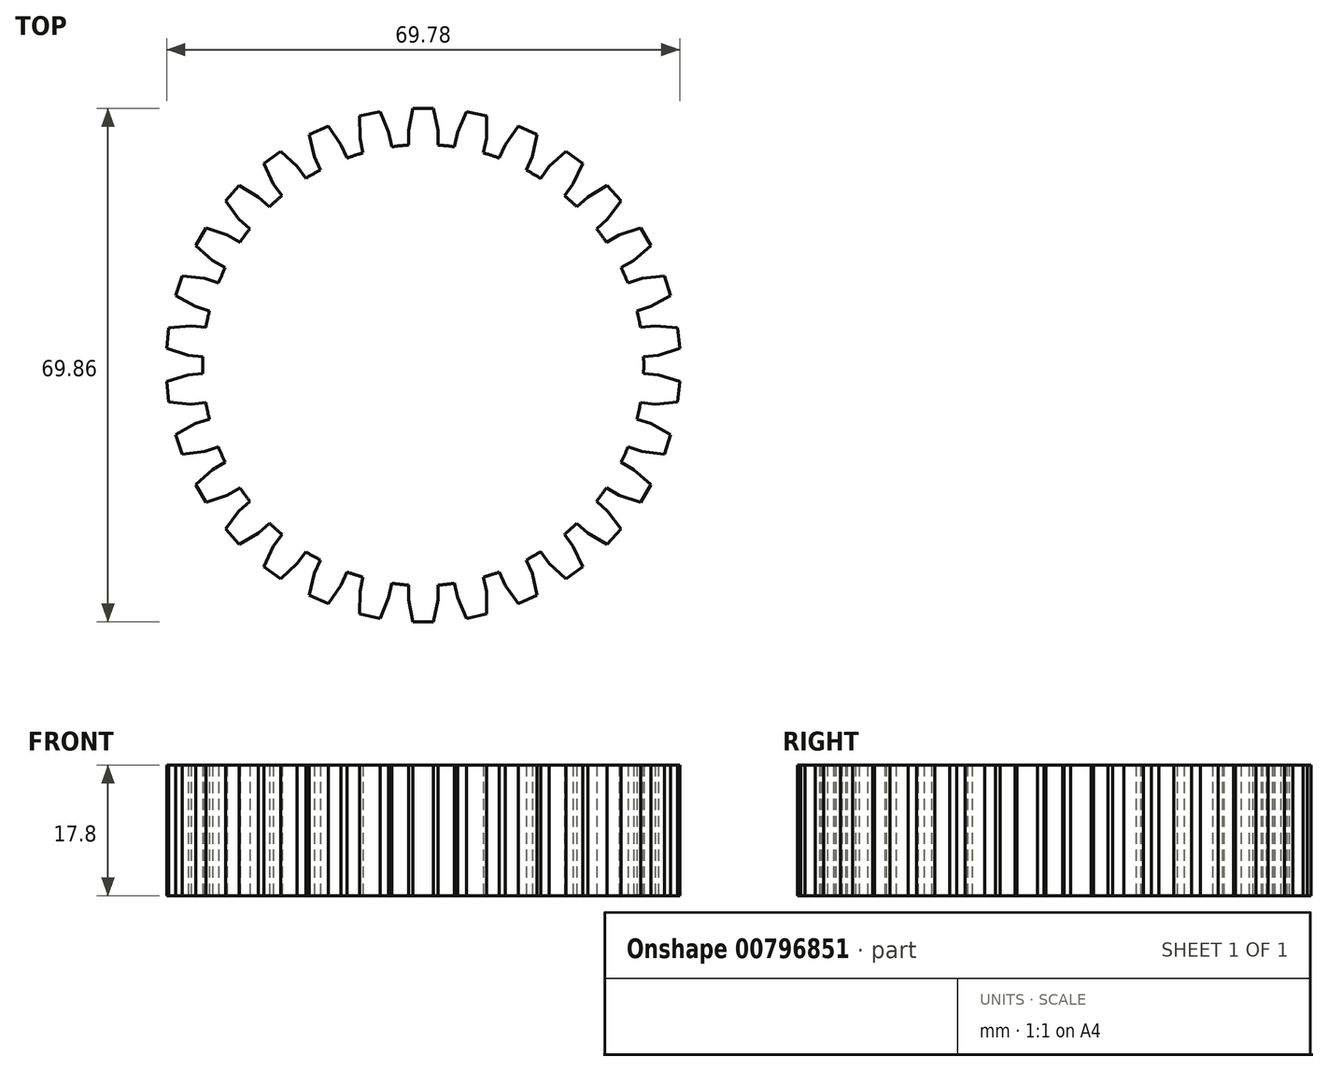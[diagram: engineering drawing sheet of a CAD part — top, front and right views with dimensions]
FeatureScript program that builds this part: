
annotation { "Feature Type Name" : "Feature", "Feature Type Description" : "" }
export const myFeature = defineFeature(function(context is Context, id is Id, definition is map)
    precondition{}
    {
        {
            var Q0;
            Q0=qCreatedBy(makeId("Top.planeOp"),FACE);
            var sketch = newSketch(context, id + "F0", { "sketchPlane" : qUnion([Q0])});
            skArc(sketch, "E0", {"start": v(-23.58, 18.54) * mm, "mid": v(-24.27, 17.63) * mm, "end": v(-24.92, 16.7) * mm});
            skLineSegment(sketch, "E1", {"start": v(1.41, 34.93) * mm, "end": v(-1.41, 34.93) * mm});
            skLineSegment(sketch, "E2", {"start": v(-2, 31.93) * mm, "end": v(-2, 29.93) * mm});
            skLineSegment(sketch, "E3", {"start": v(2, 31.93) * mm, "end": v(2, 29.93) * mm});
            skLineSegment(sketch, "E4", {"start": v(-2, 31.93) * mm, "end": v(-1.41, 34.93) * mm});
            skLineSegment(sketch, "E5.MirrorCS", {"start": v(2, 31.93) * mm, "end": v(1.41, 34.93) * mm});
            skPoint(sketch, "E6.orphan", {"position": v(-1.36, 35.2) * mm});
            skPoint(sketch, "E7.orphan", {"position": v(1.36, 35.2) * mm});
            skPoint(sketch, "E8.1.0", {"position": v(-8.65, 34.15) * mm});
            skLineSegment(sketch, "E8.1.1", {"start": v(-4.68, 31.65) * mm, "end": v(-5.88, 34.46) * mm});
            skLineSegment(sketch, "E8.1.2", {"start": v(-8.6, 30.82) * mm, "end": v(-8.64, 33.88) * mm});
            skLineSegment(sketch, "E8.1.3", {"start": v(-4.68, 31.65) * mm, "end": v(-4.27, 29.7) * mm});
            skLineSegment(sketch, "E8.1.4", {"start": v(-8.6, 30.82) * mm, "end": v(-8.18, 28.86) * mm});
            skLineSegment(sketch, "E8.1.5", {"start": v(-5.88, 34.46) * mm, "end": v(-8.64, 33.88) * mm});
            skPoint(sketch, "E8.1.6", {"position": v(-5.99, 34.71) * mm});
            skPoint(sketch, "E8.2.0", {"position": v(-15.56, 31.6) * mm});
            skLineSegment(sketch, "E8.2.1", {"start": v(-11.16, 29.99) * mm, "end": v(-12.92, 32.49) * mm});
            skLineSegment(sketch, "E8.2.2", {"start": v(-14.82, 28.36) * mm, "end": v(-15.5, 31.34) * mm});
            skLineSegment(sketch, "E8.2.3", {"start": v(-11.16, 29.99) * mm, "end": v(-10.35, 28.16) * mm});
            skLineSegment(sketch, "E8.2.4", {"start": v(-14.82, 28.36) * mm, "end": v(-14, 26.53) * mm});
            skLineSegment(sketch, "E8.2.5", {"start": v(-12.92, 32.49) * mm, "end": v(-15.5, 31.34) * mm});
            skPoint(sketch, "E8.2.6", {"position": v(-13.08, 32.7) * mm});
            skPoint(sketch, "E8.3.0", {"position": v(-21.79, 27.68) * mm});
            skLineSegment(sketch, "E8.3.1", {"start": v(-17.15, 27.01) * mm, "end": v(-19.4, 29.1) * mm});
            skLineSegment(sketch, "E8.3.2", {"start": v(-20.39, 24.66) * mm, "end": v(-21.67, 27.43) * mm});
            skLineSegment(sketch, "E8.3.3", {"start": v(-17.15, 27.01) * mm, "end": v(-15.98, 25.4) * mm});
            skLineSegment(sketch, "E8.3.4", {"start": v(-20.39, 24.66) * mm, "end": v(-19.21, 23.04) * mm});
            skLineSegment(sketch, "E8.3.5", {"start": v(-19.4, 29.1) * mm, "end": v(-21.67, 27.43) * mm});
            skPoint(sketch, "E8.3.6", {"position": v(-19.6, 29.27) * mm});
            skPoint(sketch, "E8.4.0", {"position": v(-27.07, 22.54) * mm});
            skLineSegment(sketch, "E8.4.1", {"start": v(-22.4, 22.85) * mm, "end": v(-25.02, 24.42) * mm});
            skLineSegment(sketch, "E8.4.2", {"start": v(-25.07, 19.88) * mm, "end": v(-26.9, 22.33) * mm});
            skLineSegment(sketch, "E8.4.3", {"start": v(-22.4, 22.85) * mm, "end": v(-20.9, 21.52) * mm});
            skLineSegment(sketch, "E8.4.4", {"start": v(-25.07, 19.88) * mm, "end": v(-23.58, 18.54) * mm});
            skLineSegment(sketch, "E8.4.5", {"start": v(-25.02, 24.42) * mm, "end": v(-26.9, 22.33) * mm});
            skPoint(sketch, "E8.4.6", {"position": v(-25.25, 24.56) * mm});
            skPoint(sketch, "E8.5.0", {"position": v(-31.16, 16.42) * mm});
            skLineSegment(sketch, "E8.5.1", {"start": v(-26.66, 17.7) * mm, "end": v(-29.55, 18.69) * mm});
            skLineSegment(sketch, "E8.5.2", {"start": v(-28.66, 14.23) * mm, "end": v(-30.96, 16.25) * mm});
            skLineSegment(sketch, "E8.5.3", {"start": v(-26.66, 17.7) * mm, "end": v(-24.92, 16.7) * mm});
            skLineSegment(sketch, "E8.5.4", {"start": v(-28.66, 14.23) * mm, "end": v(-26.92, 13.23) * mm});
            skLineSegment(sketch, "E8.5.5", {"start": v(-29.55, 18.69) * mm, "end": v(-30.96, 16.25) * mm});
            skPoint(sketch, "E8.5.6", {"position": v(-29.8, 18.78) * mm});
            skPoint(sketch, "E8.6.0", {"position": v(-33.9, 9.59) * mm});
            skLineSegment(sketch, "E8.6.1", {"start": v(-29.75, 11.77) * mm, "end": v(-32.79, 12.14) * mm});
            skLineSegment(sketch, "E8.6.2", {"start": v(-30.99, 7.97) * mm, "end": v(-33.66, 9.45) * mm});
            skLineSegment(sketch, "E8.6.3", {"start": v(-29.75, 11.77) * mm, "end": v(-27.85, 11.15) * mm});
            skLineSegment(sketch, "E8.6.4", {"start": v(-30.99, 7.97) * mm, "end": v(-29.09, 7.35) * mm});
            skLineSegment(sketch, "E8.6.5", {"start": v(-32.79, 12.14) * mm, "end": v(-33.66, 9.45) * mm});
            skPoint(sketch, "E8.6.6", {"position": v(-33.06, 12.17) * mm});
            skPoint(sketch, "E8.7.0", {"position": v(-35.15, 2.33) * mm});
            skLineSegment(sketch, "E8.7.1", {"start": v(-31.55, 5.33) * mm, "end": v(-34.6, 5.05) * mm});
            skLineSegment(sketch, "E8.7.2", {"start": v(-31.97, 1.35) * mm, "end": v(-34.89, 2.25) * mm});
            skLineSegment(sketch, "E8.7.3", {"start": v(-31.55, 5.33) * mm, "end": v(-29.56, 5.12) * mm});
            skLineSegment(sketch, "E8.7.4", {"start": v(-31.97, 1.35) * mm, "end": v(-29.98, 1.14) * mm});
            skLineSegment(sketch, "E8.7.5", {"start": v(-34.6, 5.05) * mm, "end": v(-34.89, 2.25) * mm});
            skPoint(sketch, "E8.7.6", {"position": v(-34.86, 5.03) * mm});
            skPoint(sketch, "E8.8.0", {"position": v(-34.86, -5.03) * mm});
            skLineSegment(sketch, "E8.8.1", {"start": v(-31.97, -1.35) * mm, "end": v(-34.89, -2.25) * mm});
            skLineSegment(sketch, "E8.8.2", {"start": v(-31.55, -5.33) * mm, "end": v(-34.6, -5.05) * mm});
            skLineSegment(sketch, "E8.8.3", {"start": v(-31.97, -1.35) * mm, "end": v(-29.98, -1.14) * mm});
            skLineSegment(sketch, "E8.8.4", {"start": v(-31.55, -5.33) * mm, "end": v(-29.56, -5.12) * mm});
            skLineSegment(sketch, "E8.8.5", {"start": v(-34.89, -2.25) * mm, "end": v(-34.6, -5.05) * mm});
            skPoint(sketch, "E8.8.6", {"position": v(-35.15, -2.33) * mm});
            skPoint(sketch, "E8.9.0", {"position": v(-33.06, -12.17) * mm});
            skLineSegment(sketch, "E8.9.1", {"start": v(-30.99, -7.97) * mm, "end": v(-33.66, -9.45) * mm});
            skLineSegment(sketch, "E8.9.2", {"start": v(-29.75, -11.77) * mm, "end": v(-32.79, -12.14) * mm});
            skLineSegment(sketch, "E8.9.3", {"start": v(-30.99, -7.97) * mm, "end": v(-29.09, -7.35) * mm});
            skLineSegment(sketch, "E8.9.4", {"start": v(-29.75, -11.77) * mm, "end": v(-27.85, -11.15) * mm});
            skLineSegment(sketch, "E8.9.5", {"start": v(-33.66, -9.45) * mm, "end": v(-32.79, -12.14) * mm});
            skPoint(sketch, "E8.9.6", {"position": v(-33.9, -9.59) * mm});
            skPoint(sketch, "E8.10.0", {"position": v(-29.8, -18.78) * mm});
            skLineSegment(sketch, "E8.10.1", {"start": v(-28.66, -14.23) * mm, "end": v(-30.96, -16.25) * mm});
            skLineSegment(sketch, "E8.10.2", {"start": v(-26.66, -17.7) * mm, "end": v(-29.55, -18.69) * mm});
            skLineSegment(sketch, "E8.10.3", {"start": v(-28.66, -14.23) * mm, "end": v(-26.92, -13.23) * mm});
            skLineSegment(sketch, "E8.10.4", {"start": v(-26.66, -17.7) * mm, "end": v(-24.92, -16.7) * mm});
            skLineSegment(sketch, "E8.10.5", {"start": v(-30.96, -16.25) * mm, "end": v(-29.55, -18.69) * mm});
            skPoint(sketch, "E8.10.6", {"position": v(-31.16, -16.42) * mm});
            skPoint(sketch, "E8.11.0", {"position": v(-25.25, -24.56) * mm});
            skLineSegment(sketch, "E8.11.1", {"start": v(-25.07, -19.88) * mm, "end": v(-26.9, -22.33) * mm});
            skLineSegment(sketch, "E8.11.2", {"start": v(-22.4, -22.85) * mm, "end": v(-25.02, -24.42) * mm});
            skLineSegment(sketch, "E8.11.3", {"start": v(-25.07, -19.88) * mm, "end": v(-23.58, -18.54) * mm});
            skLineSegment(sketch, "E8.11.4", {"start": v(-22.4, -22.85) * mm, "end": v(-20.9, -21.52) * mm});
            skLineSegment(sketch, "E8.11.5", {"start": v(-26.9, -22.33) * mm, "end": v(-25.02, -24.42) * mm});
            skPoint(sketch, "E8.11.6", {"position": v(-27.07, -22.54) * mm});
            skPoint(sketch, "E8.12.0", {"position": v(-19.6, -29.27) * mm});
            skLineSegment(sketch, "E8.12.1", {"start": v(-20.39, -24.66) * mm, "end": v(-21.67, -27.43) * mm});
            skLineSegment(sketch, "E8.12.2", {"start": v(-17.15, -27.01) * mm, "end": v(-19.4, -29.1) * mm});
            skLineSegment(sketch, "E8.12.3", {"start": v(-20.39, -24.66) * mm, "end": v(-19.21, -23.04) * mm});
            skLineSegment(sketch, "E8.12.4", {"start": v(-17.15, -27.01) * mm, "end": v(-15.98, -25.4) * mm});
            skLineSegment(sketch, "E8.12.5", {"start": v(-21.67, -27.43) * mm, "end": v(-19.4, -29.1) * mm});
            skPoint(sketch, "E8.12.6", {"position": v(-21.79, -27.68) * mm});
            skPoint(sketch, "E8.13.0", {"position": v(-13.08, -32.7) * mm});
            skLineSegment(sketch, "E8.13.1", {"start": v(-14.82, -28.36) * mm, "end": v(-15.5, -31.34) * mm});
            skLineSegment(sketch, "E8.13.2", {"start": v(-11.16, -29.99) * mm, "end": v(-12.92, -32.49) * mm});
            skLineSegment(sketch, "E8.13.3", {"start": v(-14.82, -28.36) * mm, "end": v(-14, -26.53) * mm});
            skLineSegment(sketch, "E8.13.4", {"start": v(-11.16, -29.99) * mm, "end": v(-10.35, -28.16) * mm});
            skLineSegment(sketch, "E8.13.5", {"start": v(-15.5, -31.34) * mm, "end": v(-12.92, -32.49) * mm});
            skPoint(sketch, "E8.13.6", {"position": v(-15.56, -31.6) * mm});
            skPoint(sketch, "E8.14.0", {"position": v(-5.99, -34.71) * mm});
            skLineSegment(sketch, "E8.14.1", {"start": v(-8.6, -30.82) * mm, "end": v(-8.64, -33.88) * mm});
            skLineSegment(sketch, "E8.14.2", {"start": v(-4.68, -31.65) * mm, "end": v(-5.88, -34.46) * mm});
            skLineSegment(sketch, "E8.14.3", {"start": v(-8.6, -30.82) * mm, "end": v(-8.18, -28.86) * mm});
            skLineSegment(sketch, "E8.14.4", {"start": v(-4.68, -31.65) * mm, "end": v(-4.27, -29.7) * mm});
            skLineSegment(sketch, "E8.14.5", {"start": v(-8.64, -33.88) * mm, "end": v(-5.88, -34.46) * mm});
            skPoint(sketch, "E8.14.6", {"position": v(-8.65, -34.15) * mm});
            skPoint(sketch, "E8.15.0", {"position": v(1.36, -35.2) * mm});
            skLineSegment(sketch, "E8.15.1", {"start": v(-2, -31.93) * mm, "end": v(-1.41, -34.93) * mm});
            skLineSegment(sketch, "E8.15.2", {"start": v(2, -31.93) * mm, "end": v(1.41, -34.93) * mm});
            skLineSegment(sketch, "E8.15.3", {"start": v(-2, -31.93) * mm, "end": v(-2, -29.93) * mm});
            skLineSegment(sketch, "E8.15.4", {"start": v(2, -31.93) * mm, "end": v(2, -29.93) * mm});
            skLineSegment(sketch, "E8.15.5", {"start": v(-1.41, -34.93) * mm, "end": v(1.41, -34.93) * mm});
            skPoint(sketch, "E8.15.6", {"position": v(-1.36, -35.2) * mm});
            skPoint(sketch, "E8.16.0", {"position": v(8.65, -34.15) * mm});
            skLineSegment(sketch, "E8.16.1", {"start": v(4.68, -31.65) * mm, "end": v(5.88, -34.46) * mm});
            skLineSegment(sketch, "E8.16.2", {"start": v(8.6, -30.82) * mm, "end": v(8.64, -33.88) * mm});
            skLineSegment(sketch, "E8.16.3", {"start": v(4.68, -31.65) * mm, "end": v(4.27, -29.7) * mm});
            skLineSegment(sketch, "E8.16.4", {"start": v(8.6, -30.82) * mm, "end": v(8.18, -28.86) * mm});
            skLineSegment(sketch, "E8.16.5", {"start": v(5.88, -34.46) * mm, "end": v(8.64, -33.88) * mm});
            skPoint(sketch, "E8.16.6", {"position": v(5.99, -34.71) * mm});
            skPoint(sketch, "E8.17.0", {"position": v(15.56, -31.6) * mm});
            skLineSegment(sketch, "E8.17.1", {"start": v(11.16, -29.99) * mm, "end": v(12.92, -32.49) * mm});
            skLineSegment(sketch, "E8.17.2", {"start": v(14.82, -28.36) * mm, "end": v(15.5, -31.34) * mm});
            skLineSegment(sketch, "E8.17.3", {"start": v(11.16, -29.99) * mm, "end": v(10.35, -28.16) * mm});
            skLineSegment(sketch, "E8.17.4", {"start": v(14.82, -28.36) * mm, "end": v(14, -26.53) * mm});
            skLineSegment(sketch, "E8.17.5", {"start": v(12.92, -32.49) * mm, "end": v(15.5, -31.34) * mm});
            skPoint(sketch, "E8.17.6", {"position": v(13.08, -32.7) * mm});
            skPoint(sketch, "E8.18.0", {"position": v(21.79, -27.68) * mm});
            skLineSegment(sketch, "E8.18.1", {"start": v(17.15, -27.01) * mm, "end": v(19.4, -29.1) * mm});
            skLineSegment(sketch, "E8.18.2", {"start": v(20.39, -24.66) * mm, "end": v(21.67, -27.43) * mm});
            skLineSegment(sketch, "E8.18.3", {"start": v(17.15, -27.01) * mm, "end": v(15.98, -25.4) * mm});
            skLineSegment(sketch, "E8.18.4", {"start": v(20.39, -24.66) * mm, "end": v(19.21, -23.04) * mm});
            skLineSegment(sketch, "E8.18.5", {"start": v(19.4, -29.1) * mm, "end": v(21.67, -27.43) * mm});
            skPoint(sketch, "E8.18.6", {"position": v(19.6, -29.27) * mm});
            skPoint(sketch, "E8.19.0", {"position": v(27.07, -22.54) * mm});
            skLineSegment(sketch, "E8.19.1", {"start": v(22.4, -22.85) * mm, "end": v(25.02, -24.42) * mm});
            skLineSegment(sketch, "E8.19.2", {"start": v(25.07, -19.88) * mm, "end": v(26.9, -22.33) * mm});
            skLineSegment(sketch, "E8.19.3", {"start": v(22.4, -22.85) * mm, "end": v(20.9, -21.52) * mm});
            skLineSegment(sketch, "E8.19.4", {"start": v(25.07, -19.88) * mm, "end": v(23.58, -18.54) * mm});
            skLineSegment(sketch, "E8.19.5", {"start": v(25.02, -24.42) * mm, "end": v(26.9, -22.33) * mm});
            skPoint(sketch, "E8.19.6", {"position": v(25.25, -24.56) * mm});
            skPoint(sketch, "E8.20.0", {"position": v(31.16, -16.42) * mm});
            skLineSegment(sketch, "E8.20.1", {"start": v(26.66, -17.7) * mm, "end": v(29.55, -18.69) * mm});
            skLineSegment(sketch, "E8.20.2", {"start": v(28.66, -14.23) * mm, "end": v(30.96, -16.25) * mm});
            skLineSegment(sketch, "E8.20.3", {"start": v(26.66, -17.7) * mm, "end": v(24.92, -16.7) * mm});
            skLineSegment(sketch, "E8.20.4", {"start": v(28.66, -14.23) * mm, "end": v(26.92, -13.23) * mm});
            skLineSegment(sketch, "E8.20.5", {"start": v(29.55, -18.69) * mm, "end": v(30.96, -16.25) * mm});
            skPoint(sketch, "E8.20.6", {"position": v(29.8, -18.78) * mm});
            skPoint(sketch, "E8.21.0", {"position": v(33.9, -9.59) * mm});
            skLineSegment(sketch, "E8.21.1", {"start": v(29.75, -11.77) * mm, "end": v(32.79, -12.14) * mm});
            skLineSegment(sketch, "E8.21.2", {"start": v(30.99, -7.97) * mm, "end": v(33.66, -9.45) * mm});
            skLineSegment(sketch, "E8.21.3", {"start": v(29.75, -11.77) * mm, "end": v(27.85, -11.15) * mm});
            skLineSegment(sketch, "E8.21.4", {"start": v(30.99, -7.97) * mm, "end": v(29.09, -7.35) * mm});
            skLineSegment(sketch, "E8.21.5", {"start": v(32.79, -12.14) * mm, "end": v(33.66, -9.45) * mm});
            skPoint(sketch, "E8.21.6", {"position": v(33.06, -12.17) * mm});
            skPoint(sketch, "E8.22.0", {"position": v(35.15, -2.33) * mm});
            skLineSegment(sketch, "E8.22.1", {"start": v(31.55, -5.33) * mm, "end": v(34.6, -5.05) * mm});
            skLineSegment(sketch, "E8.22.2", {"start": v(31.97, -1.35) * mm, "end": v(34.89, -2.25) * mm});
            skLineSegment(sketch, "E8.22.3", {"start": v(31.55, -5.33) * mm, "end": v(29.56, -5.12) * mm});
            skLineSegment(sketch, "E8.22.4", {"start": v(31.97, -1.35) * mm, "end": v(29.98, -1.14) * mm});
            skLineSegment(sketch, "E8.22.5", {"start": v(34.6, -5.05) * mm, "end": v(34.89, -2.25) * mm});
            skPoint(sketch, "E8.22.6", {"position": v(34.86, -5.03) * mm});
            skPoint(sketch, "E8.23.0", {"position": v(34.86, 5.03) * mm});
            skLineSegment(sketch, "E8.23.1", {"start": v(31.97, 1.35) * mm, "end": v(34.89, 2.25) * mm});
            skLineSegment(sketch, "E8.23.2", {"start": v(31.55, 5.33) * mm, "end": v(34.6, 5.05) * mm});
            skLineSegment(sketch, "E8.23.3", {"start": v(31.97, 1.35) * mm, "end": v(29.98, 1.14) * mm});
            skLineSegment(sketch, "E8.23.4", {"start": v(31.55, 5.33) * mm, "end": v(29.56, 5.12) * mm});
            skLineSegment(sketch, "E8.23.5", {"start": v(34.89, 2.25) * mm, "end": v(34.6, 5.05) * mm});
            skPoint(sketch, "E8.23.6", {"position": v(35.15, 2.33) * mm});
            skPoint(sketch, "E8.24.0", {"position": v(33.06, 12.17) * mm});
            skLineSegment(sketch, "E8.24.1", {"start": v(30.99, 7.97) * mm, "end": v(33.66, 9.45) * mm});
            skLineSegment(sketch, "E8.24.2", {"start": v(29.75, 11.77) * mm, "end": v(32.79, 12.14) * mm});
            skLineSegment(sketch, "E8.24.3", {"start": v(30.99, 7.97) * mm, "end": v(29.09, 7.35) * mm});
            skLineSegment(sketch, "E8.24.4", {"start": v(29.75, 11.77) * mm, "end": v(27.85, 11.15) * mm});
            skLineSegment(sketch, "E8.24.5", {"start": v(33.66, 9.45) * mm, "end": v(32.79, 12.14) * mm});
            skPoint(sketch, "E8.24.6", {"position": v(33.9, 9.59) * mm});
            skPoint(sketch, "E8.25.0", {"position": v(29.8, 18.78) * mm});
            skLineSegment(sketch, "E8.25.1", {"start": v(28.66, 14.23) * mm, "end": v(30.96, 16.25) * mm});
            skLineSegment(sketch, "E8.25.2", {"start": v(26.66, 17.7) * mm, "end": v(29.55, 18.69) * mm});
            skLineSegment(sketch, "E8.25.3", {"start": v(28.66, 14.23) * mm, "end": v(26.92, 13.23) * mm});
            skLineSegment(sketch, "E8.25.4", {"start": v(26.66, 17.7) * mm, "end": v(24.92, 16.7) * mm});
            skLineSegment(sketch, "E8.25.5", {"start": v(30.96, 16.25) * mm, "end": v(29.55, 18.69) * mm});
            skPoint(sketch, "E8.25.6", {"position": v(31.16, 16.42) * mm});
            skPoint(sketch, "E8.26.0", {"position": v(25.25, 24.56) * mm});
            skLineSegment(sketch, "E8.26.1", {"start": v(25.07, 19.88) * mm, "end": v(26.9, 22.33) * mm});
            skLineSegment(sketch, "E8.26.2", {"start": v(22.4, 22.85) * mm, "end": v(25.02, 24.42) * mm});
            skLineSegment(sketch, "E8.26.3", {"start": v(25.07, 19.88) * mm, "end": v(23.58, 18.54) * mm});
            skLineSegment(sketch, "E8.26.4", {"start": v(22.4, 22.85) * mm, "end": v(20.9, 21.52) * mm});
            skLineSegment(sketch, "E8.26.5", {"start": v(26.9, 22.33) * mm, "end": v(25.02, 24.42) * mm});
            skPoint(sketch, "E8.26.6", {"position": v(27.07, 22.54) * mm});
            skPoint(sketch, "E8.27.0", {"position": v(19.6, 29.27) * mm});
            skLineSegment(sketch, "E8.27.1", {"start": v(20.39, 24.66) * mm, "end": v(21.67, 27.43) * mm});
            skLineSegment(sketch, "E8.27.2", {"start": v(17.15, 27.01) * mm, "end": v(19.4, 29.1) * mm});
            skLineSegment(sketch, "E8.27.3", {"start": v(20.39, 24.66) * mm, "end": v(19.21, 23.04) * mm});
            skLineSegment(sketch, "E8.27.4", {"start": v(17.15, 27.01) * mm, "end": v(15.98, 25.4) * mm});
            skLineSegment(sketch, "E8.27.5", {"start": v(21.67, 27.43) * mm, "end": v(19.4, 29.1) * mm});
            skPoint(sketch, "E8.27.6", {"position": v(21.79, 27.68) * mm});
            skPoint(sketch, "E8.28.0", {"position": v(13.08, 32.7) * mm});
            skLineSegment(sketch, "E8.28.1", {"start": v(14.82, 28.36) * mm, "end": v(15.5, 31.34) * mm});
            skLineSegment(sketch, "E8.28.2", {"start": v(11.16, 29.99) * mm, "end": v(12.92, 32.49) * mm});
            skLineSegment(sketch, "E8.28.3", {"start": v(14.82, 28.36) * mm, "end": v(14, 26.53) * mm});
            skLineSegment(sketch, "E8.28.4", {"start": v(11.16, 29.99) * mm, "end": v(10.35, 28.16) * mm});
            skLineSegment(sketch, "E8.28.5", {"start": v(15.5, 31.34) * mm, "end": v(12.92, 32.49) * mm});
            skPoint(sketch, "E8.28.6", {"position": v(15.56, 31.6) * mm});
            skPoint(sketch, "E8.29.0", {"position": v(5.99, 34.71) * mm});
            skLineSegment(sketch, "E8.29.1", {"start": v(8.6, 30.82) * mm, "end": v(8.64, 33.88) * mm});
            skLineSegment(sketch, "E8.29.2", {"start": v(4.68, 31.65) * mm, "end": v(5.88, 34.46) * mm});
            skLineSegment(sketch, "E8.29.3", {"start": v(8.6, 30.82) * mm, "end": v(8.18, 28.86) * mm});
            skLineSegment(sketch, "E8.29.4", {"start": v(4.68, 31.65) * mm, "end": v(4.27, 29.7) * mm});
            skLineSegment(sketch, "E8.29.5", {"start": v(8.64, 33.88) * mm, "end": v(5.88, 34.46) * mm});
            skPoint(sketch, "E8.29.6", {"position": v(8.65, 34.15) * mm});
            skArc(sketch, "E9.trimOffspring", {"start": v(-19.21, 23.04) * mm, "mid": v(-20.07, 22.3) * mm, "end": v(-20.9, 21.52) * mm});
            skArc(sketch, "E10.trimOffspring", {"start": v(-14, 26.53) * mm, "mid": v(-15, 25.98) * mm, "end": v(-15.98, 25.4) * mm});
            skArc(sketch, "E11.trimOffspring", {"start": v(-8.18, 28.86) * mm, "mid": v(-9.27, 28.53) * mm, "end": v(-10.35, 28.16) * mm});
            skArc(sketch, "E12.trimOffspring", {"start": v(-2, 29.93) * mm, "mid": v(-3.14, 29.84) * mm, "end": v(-4.27, 29.7) * mm});
            skArc(sketch, "E13.trimOffspring", {"start": v(4.27, 29.7) * mm, "mid": v(3.14, 29.84) * mm, "end": v(2, 29.93) * mm});
            skArc(sketch, "E14.trimOffspring", {"start": v(10.35, 28.16) * mm, "mid": v(9.27, 28.53) * mm, "end": v(8.18, 28.86) * mm});
            skArc(sketch, "E15.trimOffspring", {"start": v(15.98, 25.4) * mm, "mid": v(15, 25.98) * mm, "end": v(14, 26.53) * mm});
            skArc(sketch, "E16.trimOffspring", {"start": v(20.9, 21.52) * mm, "mid": v(20.07, 22.3) * mm, "end": v(19.21, 23.04) * mm});
            skArc(sketch, "E17.trimOffspring", {"start": v(24.92, 16.7) * mm, "mid": v(24.27, 17.63) * mm, "end": v(23.58, 18.54) * mm});
            skArc(sketch, "E18.trimOffspring", {"start": v(27.85, 11.15) * mm, "mid": v(27.4, 12.2) * mm, "end": v(26.92, 13.23) * mm});
            skArc(sketch, "E19.trimOffspring", {"start": v(29.56, 5.12) * mm, "mid": v(29.34, 6.24) * mm, "end": v(29.09, 7.35) * mm});
            skArc(sketch, "E20.trimOffspring", {"start": v(29.98, -1.14) * mm, "mid": v(30, 0) * mm, "end": v(29.98, 1.14) * mm});
            skArc(sketch, "E21.trimOffspring", {"start": v(29.09, -7.35) * mm, "mid": v(29.34, -6.24) * mm, "end": v(29.56, -5.12) * mm});
            skArc(sketch, "E22.trimOffspring", {"start": v(26.92, -13.23) * mm, "mid": v(27.4, -12.2) * mm, "end": v(27.85, -11.15) * mm});
            skArc(sketch, "E23.trimOffspring", {"start": v(23.58, -18.54) * mm, "mid": v(24.27, -17.63) * mm, "end": v(24.92, -16.7) * mm});
            skArc(sketch, "E24.trimOffspring", {"start": v(19.21, -23.04) * mm, "mid": v(20.07, -22.3) * mm, "end": v(20.9, -21.52) * mm});
            skArc(sketch, "E25.trimOffspring", {"start": v(14, -26.53) * mm, "mid": v(15, -25.98) * mm, "end": v(15.98, -25.4) * mm});
            skArc(sketch, "E26.trimOffspring", {"start": v(8.18, -28.86) * mm, "mid": v(9.27, -28.53) * mm, "end": v(10.35, -28.16) * mm});
            skArc(sketch, "E27.trimOffspring", {"start": v(2, -29.93) * mm, "mid": v(3.14, -29.84) * mm, "end": v(4.27, -29.7) * mm});
            skArc(sketch, "E28.trimOffspring", {"start": v(-4.27, -29.7) * mm, "mid": v(-3.14, -29.84) * mm, "end": v(-2, -29.93) * mm});
            skArc(sketch, "E29.trimOffspring", {"start": v(-10.35, -28.16) * mm, "mid": v(-9.27, -28.53) * mm, "end": v(-8.18, -28.86) * mm});
            skArc(sketch, "E30.trimOffspring", {"start": v(-15.98, -25.4) * mm, "mid": v(-15, -25.98) * mm, "end": v(-14, -26.53) * mm});
            skArc(sketch, "E31.trimOffspring", {"start": v(-20.9, -21.52) * mm, "mid": v(-20.07, -22.3) * mm, "end": v(-19.21, -23.04) * mm});
            skArc(sketch, "E32.trimOffspring", {"start": v(-24.92, -16.7) * mm, "mid": v(-24.27, -17.63) * mm, "end": v(-23.58, -18.54) * mm});
            skArc(sketch, "E33.trimOffspring", {"start": v(-27.85, -11.15) * mm, "mid": v(-27.4, -12.2) * mm, "end": v(-26.92, -13.23) * mm});
            skArc(sketch, "E34.trimOffspring", {"start": v(-29.56, -5.12) * mm, "mid": v(-29.34, -6.24) * mm, "end": v(-29.09, -7.35) * mm});
            skArc(sketch, "E35.trimOffspring", {"start": v(-29.98, 1.14) * mm, "mid": v(-30, 0) * mm, "end": v(-29.98, -1.14) * mm});
            skArc(sketch, "E36.trimOffspring", {"start": v(-29.09, 7.35) * mm, "mid": v(-29.34, 6.24) * mm, "end": v(-29.56, 5.12) * mm});
            skArc(sketch, "E37.trimOffspring", {"start": v(-26.92, 13.23) * mm, "mid": v(-27.4, 12.2) * mm, "end": v(-27.85, 11.15) * mm});
            skSolve(sketch);
        }
        {
            var Q0;
            Q0=makeQuery(id+"F0.imprint","IMPRINT",FACE,{"disambiguationData":[TD([[makeQuery(id+"F0.imprint","IMPRINT",EDGE,{"derivedFrom":sQuery(id+"F0.wireOp",EDGE,"E0")}),1.0]])]});
            extrude(context, id + "F1", {"entities" : qUnion([Q0]), "depth" : 17.8 * mm, "offsetDistance" : 25 * mm});
        }
    });
